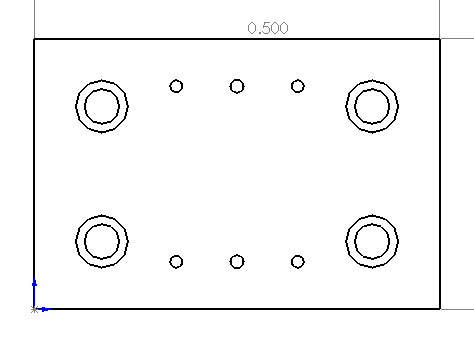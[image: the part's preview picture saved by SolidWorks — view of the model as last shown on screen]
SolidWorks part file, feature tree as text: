
SOLIDWORKS PART (.sldprt)
format: sldprt  version: not decoded by parser v0  size: 247,296 bytes
history: native  units: mm
features: sketch x5, cut_extrude x4, pattern_linear x4, material x1, extrude x1 + 1 further entry (+12 scaffold rows collapsed)
feature tree (28):
  "Annotations"  RD1=50.8mm RD2=76.2mm RD3=12.7mm
  scaffold x12  (default folders/planes/origin — collapsed)
  material  "Material <not specified>"
  sketch  "Sketch1"  dims[D1=50.8mm D2=76.2mm]
  extrude  "Extrude1"  Depth=12.7mm
  sketch  "Sketch2"  dims[D1=6.5278mm D2=12.7mm D3=12.7mm]
  cut_extrude  "Cut-Extrude1"  Depth=12.7mm
  pattern_linear  "LPattern2"  Count1=2 Count2=2 Spacing1=50.8mm Spacing2=25.4mm
  sketch  "Sketch3"  dims[D1=2.2606mm D2=8.89mm D3=26.67mm]
  cut_extrude  "Cut-Extrude2"  Depth=12.7mm
  pattern_linear  "LPattern3"  Count1=2 Count2=2 Spacing1=22.86mm Spacing2=33.02mm
  sketch  "Sketch4"  dims[D1=9.8044mm D3=10.16mm D2=12.7mm]
  cut_extrude  "Cut-Extrude3"  Depth=6.604mm
  pattern_linear  "LPattern4"  Count1=2 Count2=2 Spacing1=50.8mm Spacing2=25.4mm
  sketch  "Sketch6"  dims[c1.D2=2.4384mm c1.D1=38.1mm c2.D2=~8.475324mm c2.D3=8.89mm c2.D4=8.89mm]
  cut_extrude  "Cut-Extrude4"  Depth=7.62mm
  pattern_linear  "LPattern5"  Count1=2 Count2=1 Spacing1=33.02mm Spacing2=25.4mm
decode coverage: 14 of 14 modeling features carry decoded parameters; 1 rows unclassified (native names shown)
note: ~ marks probable driven/reference dimensions
note: suppression state not decoded; provenance and decode notes live in map.json
